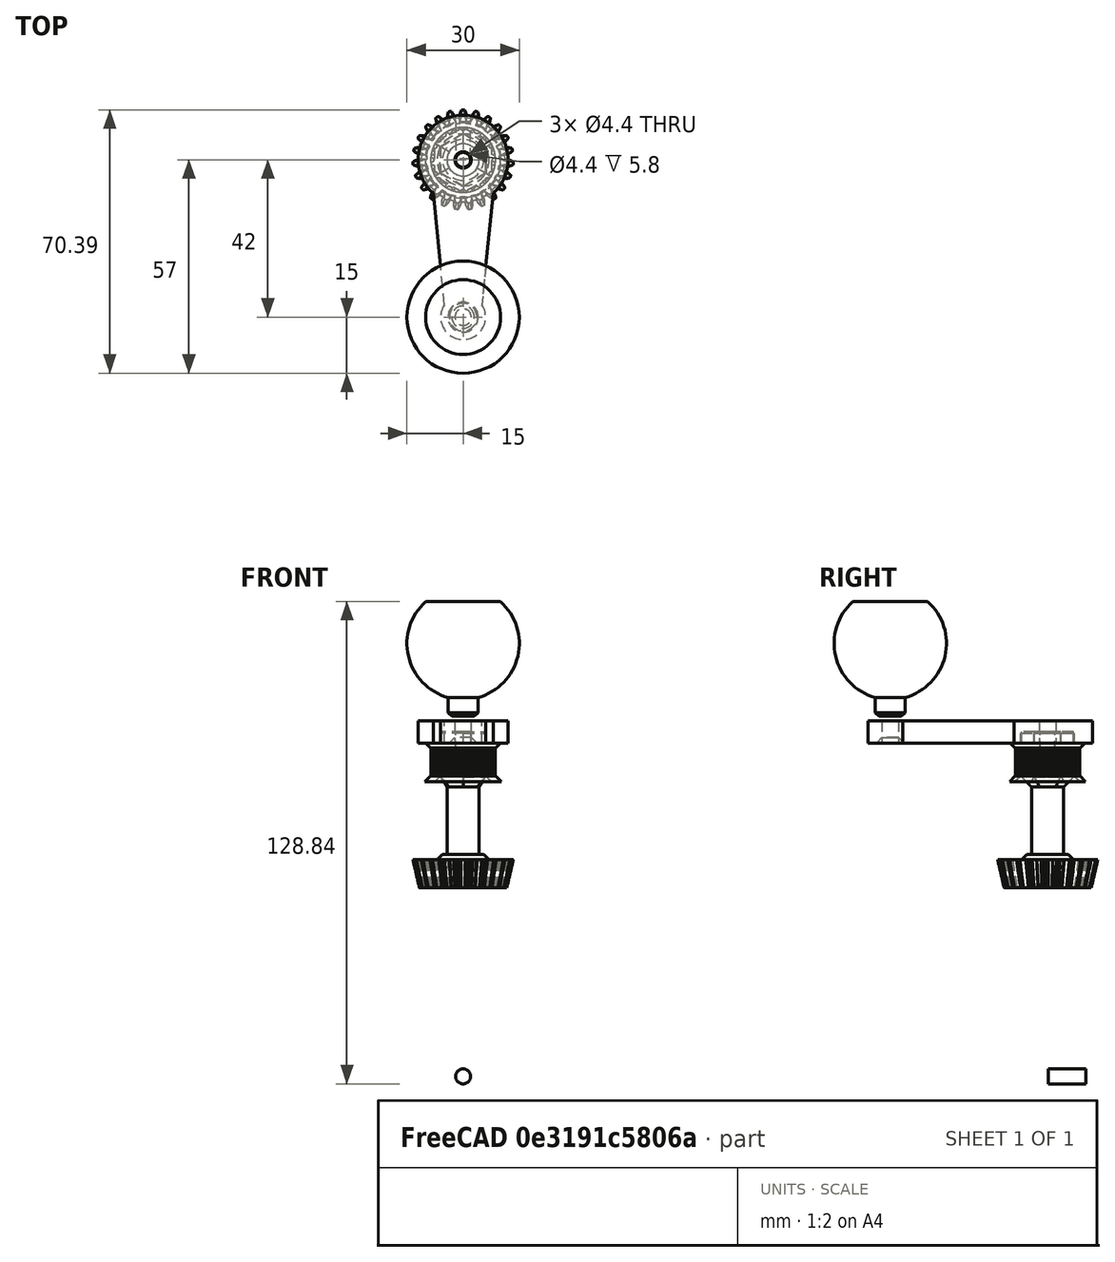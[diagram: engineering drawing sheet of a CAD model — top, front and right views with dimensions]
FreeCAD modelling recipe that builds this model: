
FCSTD DOCUMENT  (FreeCAD 0.16RUnknown)
Label: motorattach
License: All rights reserved
LicenseURL: http://en.wikipedia.org/wiki/All_rights_reserved
objects: Sketcher::SketchObject×9, Part::MultiFuse×4, PartDesign::Chamfer×3, PartDesign::Pocket×3, PartDesign::Revolution×2, PartDesign::Pad×2, Part::FeaturePython×1, Part::Loft×1
note: 32 computed .brp shape members not serialized (recipe doc carries the construction recipe); baked Part::Feature solids carry a one-line shape summary decoded from their .brp

FEATURE [Part::FeaturePython] BevelGear  label="gear"  # WARN: FeaturePython — macro-defined, semantics opaque (R4)
  backlash = 0
  clearance = 0.1
  height = 7.5
  m = 1
  numpoints = 6
  pitch_angle = 12
  pressure_angle = 20
  teeth = 23
FEATURE [Sketcher::SketchObject] Sketch  label="ref-gearprofile"
  Placement = pos=(0,0,0) rot=(1,0,0;1.5708rad)
  sketch-geometry (4):
    g0: LineSegment StartX=-13.25 StartY=7.5 StartZ=0 EndX=-11.9275 EndY=0 EndZ=0
    g1: LineSegment StartX=-11.9275 StartY=0 StartZ=0 EndX=11.9275 EndY=0 EndZ=0
    g2: LineSegment StartX=11.9275 StartY=0 StartZ=0 EndX=13.25 EndY=7.5 EndZ=0
    g3: LineSegment StartX=13.25 StartY=7.5 StartZ=0 EndX=-13.25 EndY=7.5 EndZ=0
  constraints (12):
    c: Coincident(g0,g1)
    c: PointOnObject(g1,g-1)
    c: Horizontal(g1)
    c: Coincident(g1,g2)
    c: Coincident(g2,g3)
    c: Coincident(g3,g0)
    c: Horizontal(g3)
    c: Symmetric(g1,g0,g-2)
    c: Equal(g2,g0)
    c: DistanceX(g3,g3) = 26.5
    c: DistanceY(g-1,g0) = 7.5
    c: Angle(g1,g0) = 1.74533
FEATURE [Sketcher::SketchObject] Sketch004  label="axel-profile"
  Placement = pos=(0,0,0) rot=(1,0,0;1.5708rad)
  sketch-geometry (6):
    g0: LineSegment StartX=5.5 StartY=59.3 StartZ=0 EndX=7 EndY=57.8 EndZ=0
    g1: LineSegment StartX=5.5 StartY=59.3 StartZ=0 EndX=4.3 EndY=59.3 EndZ=0
    g2: LineSegment StartX=4.3 StartY=59.3 StartZ=0 EndX=4.3 EndY=77.3 EndZ=0
    g3: LineSegment StartX=4.3 StartY=77.3 StartZ=0 EndX=0 EndY=77.3 EndZ=0
    g4: LineSegment StartX=7 StartY=57.8 StartZ=0 EndX=0 EndY=57.8 EndZ=0
    g5: LineSegment StartX=0 StartY=57.8 StartZ=0 EndX=0 EndY=77.3 EndZ=0
  constraints (18):
    c: Coincident(g1,g0)
    c: Coincident(g2,g1)
    c: Vertical(g2)
    c: Horizontal(g3)
    c: Horizontal(g1)
    c: DistanceY(g0,g1) = 1.5
    c: Angle(g1,g0) = 2.35619
    c: Coincident(g4,g0)
    c: PointOnObject(g4,g-2)
    c: Horizontal(g4)
    c: Coincident(g5,g4)
    c: Coincident(g5,g3)
    c: Vertical(g5)
    c: DistanceX(g4,g1) = 4.3
    c: DistanceX(g4,g0) = 5.5
    c: DistanceY(g4) = 57.8
    c: DistanceY(g2,g2) = 18
    c: Coincident(g3,g2)
FEATURE [PartDesign::Revolution] Revolution
  Angle = 360
  Axis = (0,0,1)
  Base = (0,0,0)
  Placement = pos=(0,0,0) rot=(1,0,0;1.5708rad)
  ReferenceAxis = -> Sketch004 [V_Axis]
  Reversed = true
  Sketch = -> Sketch004
FEATURE [Part::MultiFuse] Fusion
  Shapes = -> [Revolution,BevelGear]
FEATURE [Sketcher::SketchObject] Sketch005  label="axel-attach"
  Placement = pos=(0,0,80) rot=(0,0,1;0rad)
  sketch-geometry (7):
    g0: LineSegment StartX=0 StartY=6.9282 StartZ=0 EndX=-6 EndY=3.4641 EndZ=0
    g1: LineSegment StartX=-6 StartY=3.4641 StartZ=0 EndX=-6 EndY=-3.4641 EndZ=0
    g2: LineSegment StartX=-6 StartY=-3.4641 StartZ=0 EndX=0 EndY=-6.9282 EndZ=0
    g3: LineSegment StartX=0 StartY=-6.9282 StartZ=0 EndX=6 EndY=-3.4641 EndZ=0
    g4: LineSegment StartX=6 StartY=-3.4641 StartZ=0 EndX=6 EndY=3.4641 EndZ=0
    g5: LineSegment StartX=6 StartY=3.4641 StartZ=0 EndX=0 EndY=6.9282 EndZ=0
    g6: Circle [constr] CenterX=0 CenterY=0 CenterZ=0 NormalX=0 NormalY=0 NormalZ=1 Radius=6.9282
  constraints (16):
    c: Coincident(g0,g1)
    c: Coincident(g1,g2)
    c: Coincident(g2,g3)
    c: Coincident(g3,g4)
    c: Coincident(g4,g5)
    c: Coincident(g5,g0)
    c: Equal(g0, g1-g5) x5
    c: PointOnObject(g0,g6)
    c: PointOnObject(g1,g6)
    c: PointOnObject(g2,g6)
    c: PointOnObject(g3,g6)
    c: PointOnObject(g4,g6)
    c: PointOnObject(g5,g6)
    c: Coincident(g6,g-1)
    c: PointOnObject(g0,g-2)
    c: DistanceX(g0,g4) = 12
FEATURE [PartDesign::Pad] Pad
  Length = 12
  Length2 = 100
  Placement = pos=(0,0,80) rot=(0,0,1;0rad)
  Sketch = -> Sketch005
  Type = 0
FEATURE [Sketcher::SketchObject] Sketch006  label="axelrod-top"
  ExternalGeometry = -> [Fusion]
  Placement = pos=(0,0,77.3) rot=(0,0,1;0rad)
  Support = -> Fusion [Face5]
  sketch-geometry (2):
    g0: Circle CenterX=0 CenterY=0 CenterZ=0 NormalX=0 NormalY=0 NormalZ=1 Radius=4.3
    g1: GeomPoint [constr] X=3.83317 Y=-1.94855 Z=0
  constraints (3):
    c: Coincident(g0,g-1)
    c: PointOnObject(g1,g0)
    c: PointOnObject(g1,g-3)
FEATURE [Part::Loft] Loft
  Closed = false
  Ruled = false
  Sections = -> [Sketch006,Sketch005]
  Solid = true
FEATURE [Part::MultiFuse] Fusion001  label="gearaxel"
  Shapes = -> [Loft,Pad,Fusion]
FEATURE [Sketcher::SketchObject] Sketch007  label="crank-s"
  Placement = pos=(0,0,89) rot=(0,0,1;0rad)
  sketch-geometry (10):
    g0: ArcOfCircle CenterX=0 CenterY=0 CenterZ=0 NormalX=0 NormalY=0 NormalZ=1 Radius=12 StartAngle=5.44212 EndAngle=10.2658
    g1: LineSegment [constr] StartX=-8 StartY=-8.94427 StartZ=0 EndX=8 EndY=-8.94427 EndZ=0
    g2: LineSegment StartX=8 StartY=-8.94427 StartZ=0 EndX=5 EndY=-38.6834 EndZ=0
    g3: LineSegment [constr] StartX=5 StartY=-38.6834 StartZ=0 EndX=-5 EndY=-38.6834 EndZ=0
    g4: LineSegment StartX=-5 StartY=-38.6834 StartZ=0 EndX=-8 EndY=-8.94427 EndZ=0
    g5: ArcOfCircle CenterX=0 CenterY=-42 CenterZ=0 NormalX=0 NormalY=0 NormalZ=1 Radius=6 StartAngle=2.55591 EndAngle=6.86887
    g6: Circle CenterX=0 CenterY=-42 CenterZ=0 NormalX=0 NormalY=0 NormalZ=1 Radius=2.2
    g7: GeomPoint [constr] X=0 Y=12 Z=0
    g8: GeomPoint [constr] X=0 Y=-48 Z=0
    g9: Circle CenterX=0 CenterY=0 CenterZ=0 NormalX=0 NormalY=0 NormalZ=1 Radius=2.2
  constraints (25):
    c: Coincident(g0,g-1)
    c: Coincident(g1,g2)
    c: Coincident(g2,g3)
    c: Coincident(g3,g4)
    c: Coincident(g4,g1)
    c: Horizontal(g1)
    c: Horizontal(g3)
    c: Coincident(g1,g0)
    c: Coincident(g1,g0)
    c: PointOnObject(g5,g-2)
    c: Coincident(g5,g3)
    c: Coincident(g5,g2)
    c: DistanceX(g3,g3) = 10
    c: Radius(g0) = 12
    c: Radius(g5) = 6
    c: Coincident(g6,g5)
    c: PointOnObject(g7,g0)
    c: PointOnObject(g8,g5)
    c: PointOnObject(g8,g-2)
    c: PointOnObject(g7,g-2)
    c: DistanceY(g8,g7) = 60
    c: DistanceX(g1,g1) = 16
    c: Coincident(g9,g-1)
    c: Radius(g9) = 2.2
    c: Equal(g9,g6)
FEATURE [PartDesign::Pad] Pad001
  Length = 6
  Length2 = 100
  Placement = pos=(0,0,89) rot=(0,0,1;0rad)
  Sketch = -> Sketch007
  Type = 0
FEATURE [Sketcher::SketchObject] Sketch009  label="ball-wfoot"
  Placement = pos=(0,-42,96) rot=(0.57735,0.57735,0.57735;2.0944rad)
  sketch-geometry (5):
    g0: ArcOfCircle CenterX=0 CenterY=19.6568 CenterZ=0 NormalX=0 NormalY=0 NormalZ=1 Radius=15 StartAngle=4.98232 EndAngle=7.12425
    g1: LineSegment StartX=4 StartY=5.2 StartZ=0 EndX=4 EndY=0.2 EndZ=0
    g2: LineSegment StartX=4 StartY=0.2 StartZ=0 EndX=0 EndY=0.2 EndZ=0
    g3: LineSegment StartX=0 StartY=0.2 StartZ=0 EndX=0 EndY=30.8372 EndZ=0
    g4: LineSegment StartX=0 StartY=30.8372 StartZ=0 EndX=10 EndY=30.8372 EndZ=0
  constraints (16):
    c: Vertical(g1)
    c: Coincident(g1,g2)
    c: Coincident(g3,g2)
    c: Vertical(g3)
    c: PointOnObject(g0,g3)
    c: Radius(g0) = 15
    c: Horizontal(g2)
    c: Coincident(g0,g1)
    c: DistanceY(g1,g1) = 5
    c: DistanceX(g2,g2) = 4
    c: PointOnObject(g0,g-2)
    c: DistanceY(g-1,g2) = 0.2
    c: Coincident(g4,g3)
    c: Coincident(g4,g0)
    c: Horizontal(g4)
    c: DistanceX(g4,g4) = 10
FEATURE [PartDesign::Revolution] Revolution001
  Angle = 360
  Axis = (0,0,1)
  Base = (0,-42,96)
  Placement = pos=(0,-42,96) rot=(0.57735,0.57735,0.57735;2.0944rad)
  ReferenceAxis = -> Sketch009 [V_Axis]
  Reversed = true
  Sketch = -> Sketch009
FEATURE [PartDesign::Chamfer] Chamfer
  Base = -> Revolution001 [Edge4]
  Placement = pos=(0,-42,96) rot=(0.57735,0.57735,0.57735;2.0944rad)
  Size = 1
FEATURE [Sketcher::SketchObject] Sketch010  label="ball-hole"
  Placement = pos=(0,-42,96.2) rot=(0.707107,0.707107,0;3.14159rad)
  Support = -> Chamfer [Face1]
  sketch-geometry (1):
    g0: Circle CenterX=0 CenterY=0 CenterZ=0 NormalX=0 NormalY=0 NormalZ=1 Radius=2
  constraints (2):
    c: Coincident(g0,g-1)
    c: Radius(g0) = 2
FEATURE [PartDesign::Pocket] Pocket001  label="ball[stl]"
  Length = 10
  Placement = pos=(0,-42,96) rot=(0.57735,0.57735,0.57735;2.0944rad)
  Sketch = -> Sketch010
  Type = 0
FEATURE [Sketcher::SketchObject] Sketch012  label="axel-crankhole"
  Placement = pos=(0,0,92) rot=(0,0,1;0rad)
  Support = -> Fusion001 [Face1]
  sketch-geometry (1):
    g0: Circle CenterX=0 CenterY=0 CenterZ=0 NormalX=0 NormalY=0 NormalZ=1 Radius=2
  constraints (2):
    c: Coincident(g0,g-1)
    c: Radius(g0) = 2
FEATURE [PartDesign::Pocket] Pocket002  label="gearaxel[stl]"
  Length = 10
  Sketch = -> Sketch012
  Type = 0
FEATURE [Part::MultiFuse] union
  Placement = pos=(0,0,80.2) rot=(0,0,1;0rad)
FEATURE [Part::MultiFuse] Fusion002
  Shapes = -> [Pad001,union]
FEATURE [Sketcher::SketchObject] Sketch011  label="pulley-hole"
  Placement = pos=(0,0,78.7) rot=(1,0,0;3.14159rad)
  Support = -> Fusion002 [Face684]
  sketch-geometry (7):
    g0: LineSegment StartX=0 StartY=7.15914 StartZ=0 EndX=-6.2 EndY=3.57957 EndZ=0
    g1: LineSegment StartX=-6.2 StartY=3.57957 StartZ=0 EndX=-6.2 EndY=-3.57957 EndZ=0
    g2: LineSegment StartX=-6.2 StartY=-3.57957 StartZ=0 EndX=0 EndY=-7.15914 EndZ=0
    g3: LineSegment StartX=0 StartY=-7.15914 StartZ=0 EndX=6.2 EndY=-3.57957 EndZ=0
    g4: LineSegment StartX=6.2 StartY=-3.57957 StartZ=0 EndX=6.2 EndY=3.57957 EndZ=0
    g5: LineSegment StartX=6.2 StartY=3.57957 StartZ=0 EndX=0 EndY=7.15914 EndZ=0
    g6: Circle [constr] CenterX=0 CenterY=0 CenterZ=0 NormalX=0 NormalY=0 NormalZ=1 Radius=7.15914
  constraints (16):
    c: Coincident(g0,g1)
    c: Coincident(g1,g2)
    c: Coincident(g2,g3)
    c: Coincident(g3,g4)
    c: Coincident(g4,g5)
    c: Coincident(g5,g0)
    c: Equal(g0, g1-g5) x5
    c: PointOnObject(g0,g6)
    c: PointOnObject(g1,g6)
    c: PointOnObject(g2,g6)
    c: PointOnObject(g3,g6)
    c: PointOnObject(g4,g6)
    c: PointOnObject(g5,g6)
    c: Coincident(g6,g-1)
    c: PointOnObject(g0,g-2)
    c: DistanceX(g0,g4) = 12.4
FEATURE [PartDesign::Pocket] Pocket
  Length = 13
  Sketch = -> Sketch011
  Type = 0
FEATURE [PartDesign::Chamfer] Chamfer001  label="cr"
  Base = -> Pocket [Edge1908,Edge1905,Edge1909,Edge1913,Edge1915,Edge1912]
  Size = 1.4
FEATURE [PartDesign::Chamfer] Chamfer002  label="crank[stl]"
  Base = -> Chamfer001 [Edge695]
  Size = 1.5
